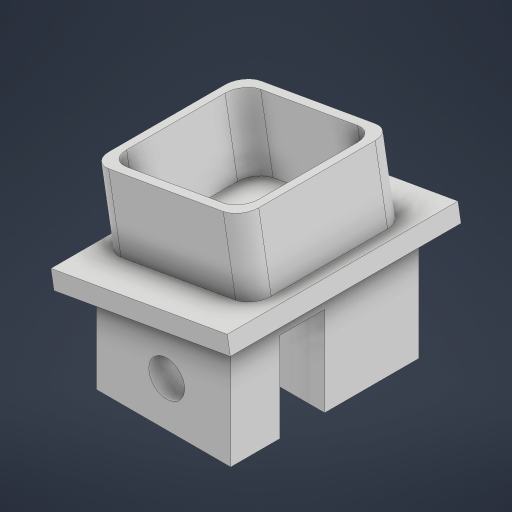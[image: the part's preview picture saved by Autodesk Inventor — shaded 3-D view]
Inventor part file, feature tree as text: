
AUTODESK INVENTOR PART (.ipt)
format: ipt  version: 2024 (Build 280153000, 153)  size: 260,608 bytes
history: native  units: mm
features: reference x11, extrude x5, sketch x5, other x4, fillet x1, projected_geometry x1
ambient origin geometry x8: Origin, YZ Plane, XZ Plane, XY Plane, X Axis, Y Axis, Z Axis, Center Point
bodies: Body1 (feature_tree)
feature tree (27):
  other  "Твердое тело1"
  extrude  "Выдавливание1"  Depth=10.0mm TaperAngle=0.0deg
  extrude  "Выдавливание2"  Depth=10.0mm TaperAngle=0.0deg
  extrude  "Выдавливание3"  Depth=1.745329mm
  extrude  "Выдавливание4"  Depth=10.0mm TaperAngle=0.0deg
  extrude  "Выдавливание5"  Depth=20.0mm
  fillet  "Сопряжение1"  Radius=2.0mm
  sketch  "Эскиз1"
  reference  "Ссылка1"
  reference  "Ссылка2"
  reference  "Ссылка3"
  reference  "Ссылка4"
  reference  "Ссылка5"
  reference  "Ссылка6"
  reference  "Ссылка7"
  reference  "Ссылка8"
  reference  "Ссылка16"
  reference  "Ссылка17"
  sketch  "Эскиз2"
  reference  "Ссылка18"
  sketch  "Эскиз3"
  sketch  "Эскиз4"
  projected_geometry  "Спроецированная петля1"
  sketch  "Эскиз5"
  parser-record x1  (decoder bookkeeping rows leaked as tree rows — omitted from the tree; the rows remain in map.json)
  other  "cum_holder_asembly.iam"
  other  "cum_holder_up:1"
note: 1 file-system path scrubbed to <path> (originals preserved in map.json)
